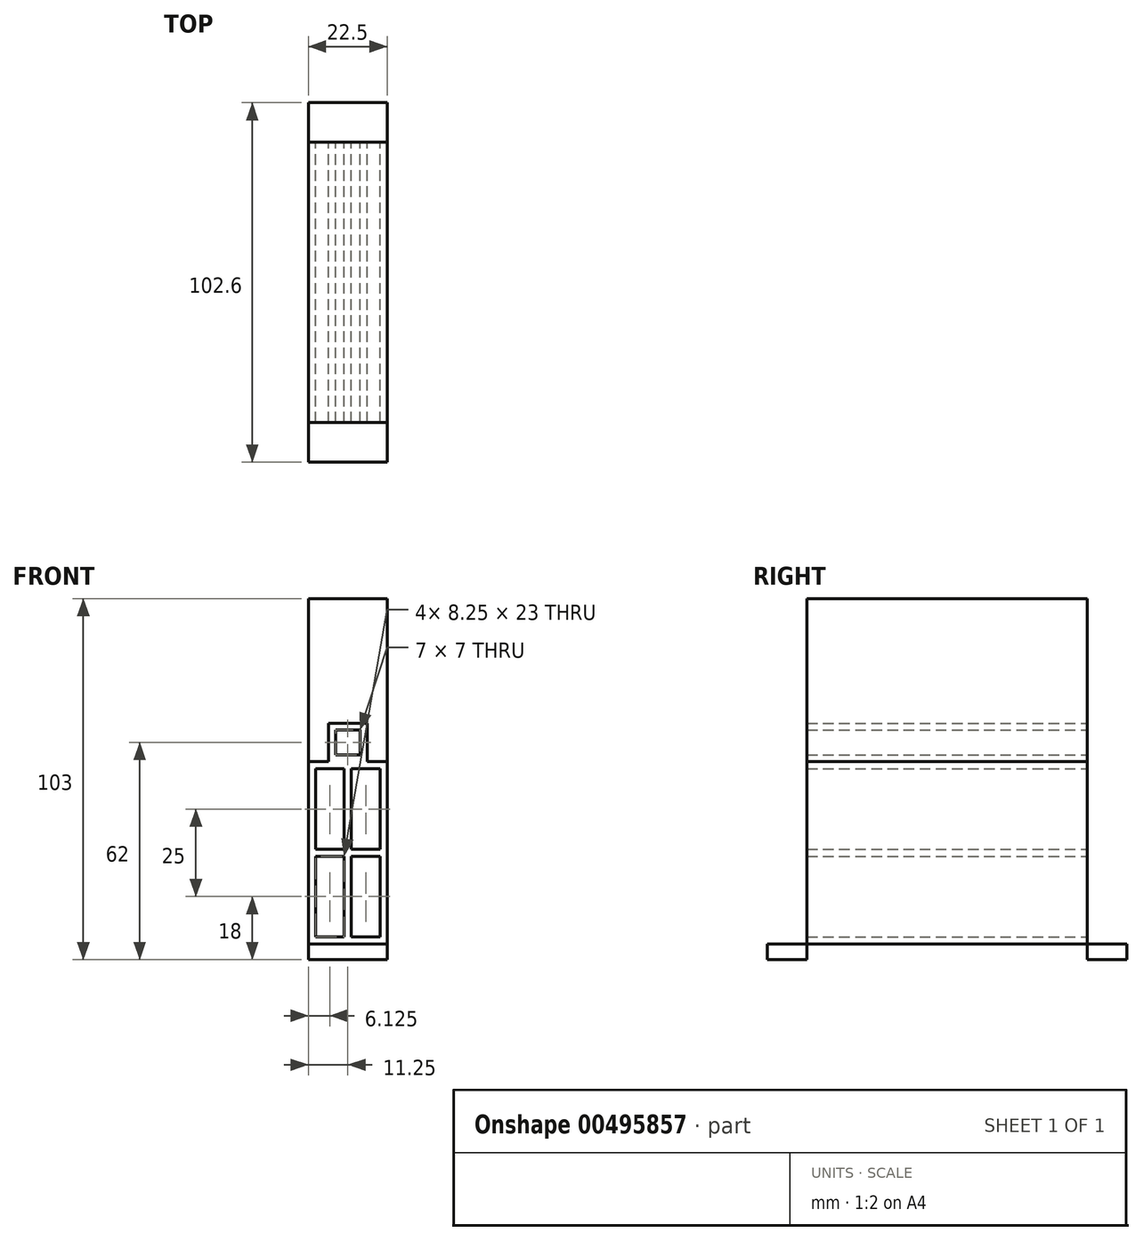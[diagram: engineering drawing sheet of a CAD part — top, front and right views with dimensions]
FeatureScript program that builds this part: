
annotation { "Feature Type Name" : "Feature", "Feature Type Description" : "" }
export const myFeature = defineFeature(function(context is Context, id is Id, definition is map)
    precondition{}
    {
        {
            var Q0;
            Q0=qCreatedBy(makeId("Front.planeOp"),FACE);
            var sketch = newSketch(context, id + "F0", { "sketchPlane" : qUnion([Q0])});
            skLineSegment(sketch, "E0.bottom", {"start": v(11.25, 26) * mm, "end": v(-11.25, 26) * mm});
            skLineSegment(sketch, "E0.top", {"start": v(11.25, -26) * mm, "end": v(-11.25, -26) * mm});
            skLineSegment(sketch, "E0.left", {"start": v(11.25, 26) * mm, "end": v(11.25, -26) * mm});
            skLineSegment(sketch, "E0.right", {"start": v(-11.25, 26) * mm, "end": v(-11.25, -26) * mm});
            skPoint(sketch, "E0.middle", {"position": v(0, 0) * mm});
            skLineSegment(sketch, "E1.bottom", {"start": v(-1, 24) * mm, "end": v(-9.25, 24) * mm});
            skLineSegment(sketch, "E1.top", {"start": v(-1, 1) * mm, "end": v(-9.25, 1) * mm});
            skLineSegment(sketch, "E1.left", {"start": v(-1, 24) * mm, "end": v(-1, 1) * mm});
            skLineSegment(sketch, "E1.right", {"start": v(-9.25, 24) * mm, "end": v(-9.25, 1) * mm});
            skPoint(sketch, "E1.middle", {"position": v(-5.13, 12.5) * mm});
            skLineSegment(sketch, "E2.MirrorCS", {"start": v(1, 1) * mm, "end": v(9.25, 1) * mm});
            skLineSegment(sketch, "E3.MirrorCS", {"start": v(9.25, 24) * mm, "end": v(9.25, 1) * mm});
            skLineSegment(sketch, "E4.MirrorCS", {"start": v(1, 24) * mm, "end": v(9.25, 24) * mm});
            skLineSegment(sketch, "E5.MirrorCS", {"start": v(1, 24) * mm, "end": v(1, 1) * mm});
            skLineSegment(sketch, "E6.MirrorCS", {"start": v(9.25, -24) * mm, "end": v(9.25, -1) * mm});
            skLineSegment(sketch, "E7.MirrorCS", {"start": v(-9.25, -24) * mm, "end": v(-9.25, -1) * mm});
            skLineSegment(sketch, "E8.MirrorCS", {"start": v(1, -24) * mm, "end": v(1, -1) * mm});
            skPoint(sketch, "E9.MirrorP", {"position": v(-5.13, -12.5) * mm});
            skLineSegment(sketch, "E10.MirrorCS", {"start": v(-1, -24) * mm, "end": v(-1, -1) * mm});
            skLineSegment(sketch, "E11.MirrorCS", {"start": v(-1, -1) * mm, "end": v(-9.25, -1) * mm});
            skLineSegment(sketch, "E12.MirrorCS", {"start": v(1, -1) * mm, "end": v(9.25, -1) * mm});
            skLineSegment(sketch, "E13.MirrorCS", {"start": v(1, -24) * mm, "end": v(9.25, -24) * mm});
            skLineSegment(sketch, "E14.MirrorCS", {"start": v(-1, -24) * mm, "end": v(-9.25, -24) * mm});
            skLineSegment(sketch, "E15.bottom", {"start": v(-5.5, 26) * mm, "end": v(5.5, 26) * mm});
            skLineSegment(sketch, "E15.top", {"start": v(-5.5, 37) * mm, "end": v(5.5, 37) * mm});
            skLineSegment(sketch, "E15.left", {"start": v(-5.5, 26) * mm, "end": v(-5.5, 37) * mm});
            skLineSegment(sketch, "E15.right", {"start": v(5.5, 26) * mm, "end": v(5.5, 37) * mm});
            skPoint(sketch, "E15.middle", {"position": v(0, 31.5) * mm});
            skLineSegment(sketch, "E16.bottom", {"start": v(3.5, 35) * mm, "end": v(-3.5, 35) * mm});
            skLineSegment(sketch, "E16.top", {"start": v(3.5, 28) * mm, "end": v(-3.5, 28) * mm});
            skLineSegment(sketch, "E16.left", {"start": v(3.5, 35) * mm, "end": v(3.5, 28) * mm});
            skLineSegment(sketch, "E16.right", {"start": v(-3.5, 35) * mm, "end": v(-3.5, 28) * mm});
            skSolve(sketch);
        }
        {
            var Q0;
            Q0=qSketchRegion(id+"F0",true);
            extrude(context, id + "F1", {"entities" : qUnion([Q0]), "depth" : 80 * mm});
        }
        {
            var Q0;
            Q0=qCreatedBy(makeId("Front.planeOp"),FACE);
            var sketch = newSketch(context, id + "F2", { "sketchPlane" : qUnion([Q0])});
            skLineSegment(sketch, "E17.0", {"start": v(-5.5, 26) * mm, "end": v(-11.25, 26) * mm});
            skLineSegment(sketch, "E18.0", {"start": v(-5.5, 26) * mm, "end": v(-5.5, 37) * mm});
            skLineSegment(sketch, "E19.0", {"start": v(-5.5, 37) * mm, "end": v(5.5, 37) * mm});
            skLineSegment(sketch, "E20.0", {"start": v(5.5, 26) * mm, "end": v(5.5, 37) * mm});
            skLineSegment(sketch, "E21.0", {"start": v(11.25, 26) * mm, "end": v(5.5, 26) * mm});
            skLineSegment(sketch, "E22", {"start": v(-11.25, 26) * mm, "end": v(-11.25, 72.5) * mm});
            skLineSegment(sketch, "E23", {"start": v(-11.25, 72.5) * mm, "end": v(11.25, 72.5) * mm});
            skLineSegment(sketch, "E24", {"start": v(11.25, 72.5) * mm, "end": v(11.25, 26) * mm});
            skSolve(sketch);
        }
        {
            var Q0;
            Q0=qSketchRegion(id+"F2",true);
            extrude(context, id + "F3", {"entities" : qUnion([Q0]), "depth" : 80 * mm});
        }
        {
            var Q0;
            Q0=makeQuery(id+"F1.opExtrude","SWEPT_FACE",FACE,{"disambiguationData":[OSD([sQuery(id+"F0.wireOp",EDGE,"E0.top")])]});
            var sketch = newSketch(context, id + "F4", { "sketchPlane" : qUnion([Q0])});
            skLineSegment(sketch, "E25.bottom", {"start": v(11.25, 0) * mm, "end": v(-11.25, 0) * mm});
            skLineSegment(sketch, "E25.top", {"start": v(11.25, -11.3) * mm, "end": v(-11.25, -11.3) * mm});
            skLineSegment(sketch, "E25.left", {"start": v(11.25, 0) * mm, "end": v(11.25, -11.3) * mm});
            skLineSegment(sketch, "E25.right", {"start": v(-11.25, 0) * mm, "end": v(-11.25, -11.3) * mm});
            skLineSegment(sketch, "E26.bottom", {"start": v(11.25, 80) * mm, "end": v(-11.25, 80) * mm});
            skLineSegment(sketch, "E26.top", {"start": v(11.25, 91.3) * mm, "end": v(-11.25, 91.3) * mm});
            skLineSegment(sketch, "E26.left", {"start": v(11.25, 80) * mm, "end": v(11.25, 91.3) * mm});
            skLineSegment(sketch, "E26.right", {"start": v(-11.25, 80) * mm, "end": v(-11.25, 91.3) * mm});
            skSolve(sketch);
        }
        {
            var Q0;
            Q0=qSketchRegion(id+"F4",true);
            extrude(context, id + "F5", {"entities" : qUnion([Q0]), "depth" : 4.5 * mm});
        }
    });
